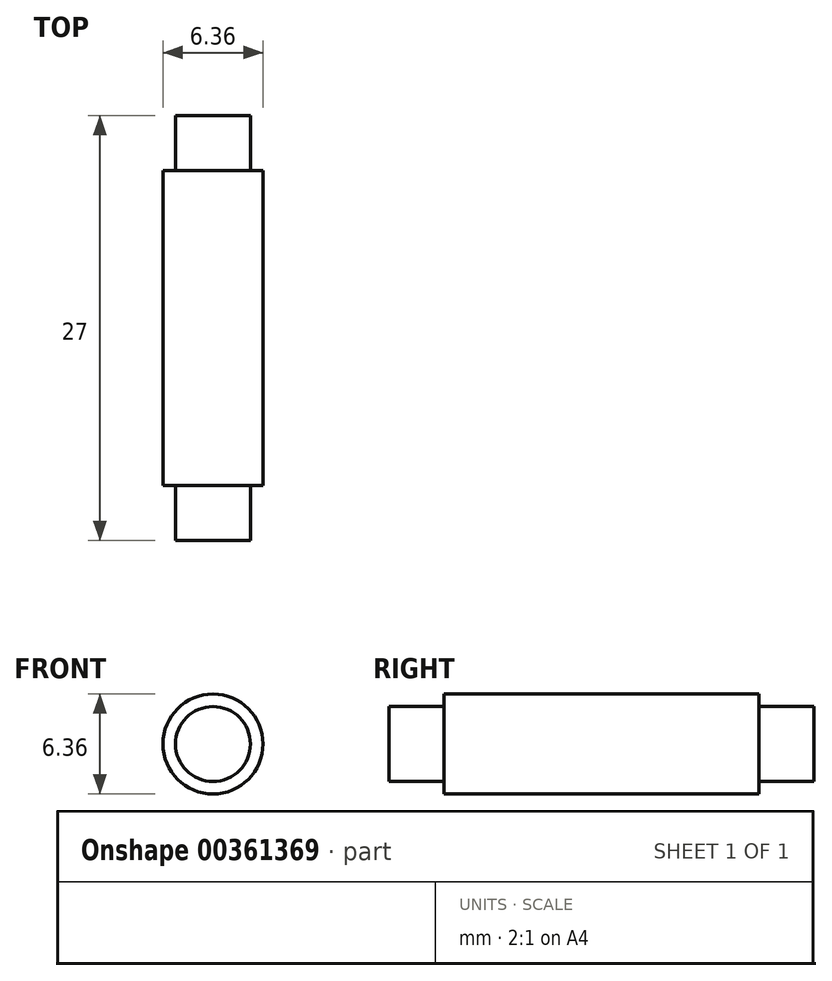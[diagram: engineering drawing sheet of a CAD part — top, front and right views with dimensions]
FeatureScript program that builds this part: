
annotation { "Feature Type Name" : "Feature", "Feature Type Description" : "" }
export const myFeature = defineFeature(function(context is Context, id is Id, definition is map)
    precondition{}
    {
        {
            var Q0;
            Q0=qCreatedBy(makeId("Front.planeOp"),FACE);
            var sketch = newSketch(context, id + "F0", { "sketchPlane" : qUnion([Q0])});
            skCircle(sketch, "E0", {"center": v(0, 0) * mm, "radius": 3.17 * mm});
            skCircle(sketch, "E1", {"center": v(0, 0) * mm, "radius": 2.38 * mm});
            skSolve(sketch);
        }
        {
            var Q0;
            Q0=makeQuery(id+"F0.imprint","IMPRINT",FACE,{"disambiguationData":[TD([[makeQuery(id+"F0.imprint","IMPRINT",EDGE,{"derivedFrom":sQuery(id+"F0.wireOp",EDGE,"E1")}),1.0]])]});
            extrude(context, id + "F1", {"entities" : qUnion([Q0]), "depth" : 27 * mm, "symmetric" : true});
        }
        {
            var Q0;
            Q0=makeQuery(id+"F0.imprint","IMPRINT",FACE,{"disambiguationData":[TD([[makeQuery(id+"F0.imprint","IMPRINT",EDGE,{"derivedFrom":sQuery(id+"F0.wireOp",EDGE,"E0")}),1.0]])]});
            extrude(context, id + "F2", {"entities" : qUnion([Q0]), "operationType" : NewBodyOperationType.ADD, "depth" : 20 * mm, "symmetric" : true});
        }
    });
